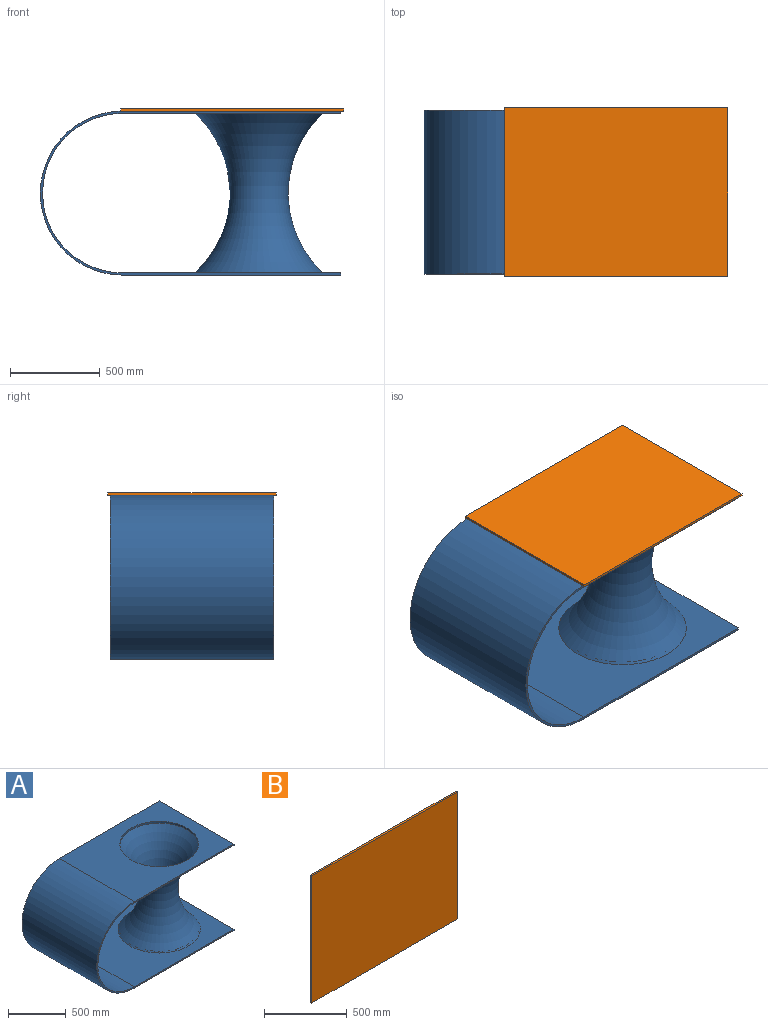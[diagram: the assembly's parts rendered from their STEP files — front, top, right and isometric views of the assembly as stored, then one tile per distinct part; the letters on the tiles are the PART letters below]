
ASSEMBLY  parts=2 mates=1
PART A: 14 faces, bbox 2055.6x1672.9x1231.9 mm
  f0: plane 914.4x12.7mm, normal (1,0,0), area 11612.9mm2, adj f1,f7,f8,f9
  f1: plane 1219.2x914.4mm, normal (0,0,1), area 751984.1mm2, adj f0,f2,f8,f9,f11
  f2: cylinder r=457.2mm len=914.4mm, axis (0,1,0), area 1313385.8mm2, adj f1,f3,f8,f9
  f3: plane 1219.2x914.4mm, normal (0,0,-1), area 1114836.5mm2, adj f2,f4,f8,f9
  f4: plane 914.4x12.7mm, normal (1,0,0), area 11612.9mm2, adj f3,f5,f8,f9
  f5: plane 1219.2x914.4mm, normal (0,0,1), area 717577.8mm2, adj f4,f6,f8,f9,f10
  f6: cylinder r=444.5mm len=914.4mm, axis (0,1,0), area 1276902.8mm2, adj f5,f7,f8,f9
  f7: plane 1219.2x914.4mm, normal (0,0,-1), area 717577.8mm2, adj f0,f6,f8,f9,f10
  f8: plane 1676.4x914.4mm, normal (0,-1,0), area 48955.8mm2, adj f0,f1,f2,f3,f4,f5,f6,f7
  f9: plane 1676.4x914.4mm, normal (0,1,0), area 48955.8mm2, adj f0,f1,f2,f3,f4,f5,f6,f7
  f10: torus R=772.77mm, axis (0,0,1), area 1432001.1mm2, adj f5,f7
  f11: cylinder r=339.85mm len=679.7mm, axis (0,0,1), area 40678.5mm2, adj f1,f13
  f12: plane 679.7x679.7mm, normal (0,0,1), area 362852.3mm2, adj f13
  f13: torus R=772.77mm, axis (0,0,1), area 1342343.6mm2, adj f11,f12
PART B: 6 faces, bbox 1244.6x12.7x939.8 mm
  f0: plane 939.8x12.7mm, normal (1,0,0), area 11935.5mm2, adj f1,f3,f4,f5
  f1: plane 1244.6x12.7mm, normal (0,0,1), area 15806.4mm2, adj f0,f2,f4,f5
  f2: plane 939.8x12.7mm, normal (-1,0,0), area 11935.5mm2, adj f1,f3,f4,f5
  f3: plane 1244.6x12.7mm, normal (0,0,-1), area 15806.4mm2, adj f0,f2,f4,f5
  f4: plane 1244.6x939.8mm, normal (0,-1,0), area 1169675.1mm2, adj f0,f1,f2,f3
  f5: plane 1244.6x939.8mm, normal (0,1,0), area 1169675.1mm2, adj f0,f1,f2,f3
PLACE A t=(-629.57,-90.95,67)mm
PLACE B rot(axis=(1,0,0),90deg) t=(97.24,8.55,536.9)mm
MATE planar B.f4 <-> A.f1  axis (0,0,-1) through (-17.31,-90.95,524.2)mm
